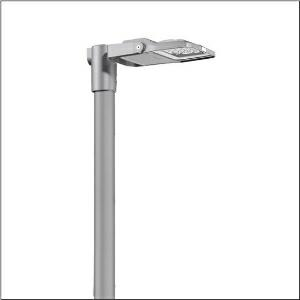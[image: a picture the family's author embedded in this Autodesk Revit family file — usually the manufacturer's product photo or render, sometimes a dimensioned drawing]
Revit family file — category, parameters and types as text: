
# Revit family: floodlight_fl_21_micro___pl43_5xa7761a4a3a_0d01
name_source: partatom
category: Lighting Fixtures
units: mm (PartAtom-declared; Revit-internal decimal feet)

## family parameters
Cut with Voids When Loaded = No
Host = Face
Light Source = No
Part Type = Normal
Room Calculation Point = No
Round Connector Dimension = Use Diameter
Shared = No

## types (1)
- --- (1 x LED, 3170 lm, 23.1 W, 4000K)
    Apparent Load = 23 VA
    CIE Flux Codes = 29 80 99 100 100
    Color Rendering = 70
    Color Temperature = 4000K
    Default Elevation = 1800 mm
    Description = Floodlight FL 21 micro, floodlight, primary light control with lens, of PMMA, primary optical cover: protective disc, of toughened safety glass, transparent, light distribution: PL43, light emission: direct distribution, installation type: surface-mounted, LED, High Power LED, rated luminous flux: 3.170lm, luminous efficacy: 137lm/W, light colour: 740, colour temperature: 4000K, control gear: ECG iQ, control: optimised constant luminous flux control (CLO 2.0), Desk-Remote (wireless, voltage-free reading and setting of iQ features in the workshop via application-optimized NFC function/RFID function), Light-Fading, Smart-Wire, Night-Set, Lumen-Switch, Temp-Guard, Auto-Match, with terminal, 6-pole, mains connection: 220..240V, AC, 50/60Hz, start of lifetime: 23W, end of lifetime: 24W, reduction: 11W, luminaire housing, of diecast aluminium, powder-coated, Siteco® metallic grey (DB 702S), corrosivity category C5 according to DIN EN ISO 12944, mast bracket, of steel, galvanised, powder-coated, Siteco® metallic grey (DB 702S), protection rating (complete): IP66, insulation class (complete): insulation class II (safety insulation), certification: CE, protection symbol: D, impact resistance: IK07, permissible operating ambient temperature: -40..+40°C, permissible operating ambient temperature for outdoor applications: -40..+50°C, standard: DIN EN 12944, packaging unit: 1 piece

Light Distribution: PL43
    Height = 65 mm
    Lamp = 1 x LED
    Lamp Light Flux = 3170 lm
    Lamp Power = 23.1 W
    Lamp count = 1
    Length = 312 mm
    Luminous efficacy = 137 lm/W
    Manufacturer = Siteco
    ModVariant = No
    Model = 5XA7761A4A3A
    Number of Poles = 1
    OnlyDefault = Yes
    Power Factor = 1
    Product Name = Floodlight FL 21 micro | PL43
    Product group = floodlight | pylon top
    ProductGroupID = 6101
    Protection Class = Protection class II
    Protection Degree = IP 66
    RLX_Detail_Level = 1
    RlxData = <blob elided: 101489 chars, md5=9ac5d41e>
    Socket = socket
    Standby Power = 0 W
    System Light Flux = 3170 lm
    System Power = 23 W
    Type Comments = factory setting: luminous flux: 100 % | dim-lin: 254 | 455 mA
    Type Image = l_1007121.jpg
    URL = http://relux.com
    VarID = @adj_090001
    Voltage = 0 V
    Weight = 0.00 kg
    Width = 230 mm

## geometry (parser evidence)
native form markers: Blend x4, Sweep x13
no freeform markers — native parametric forms only
